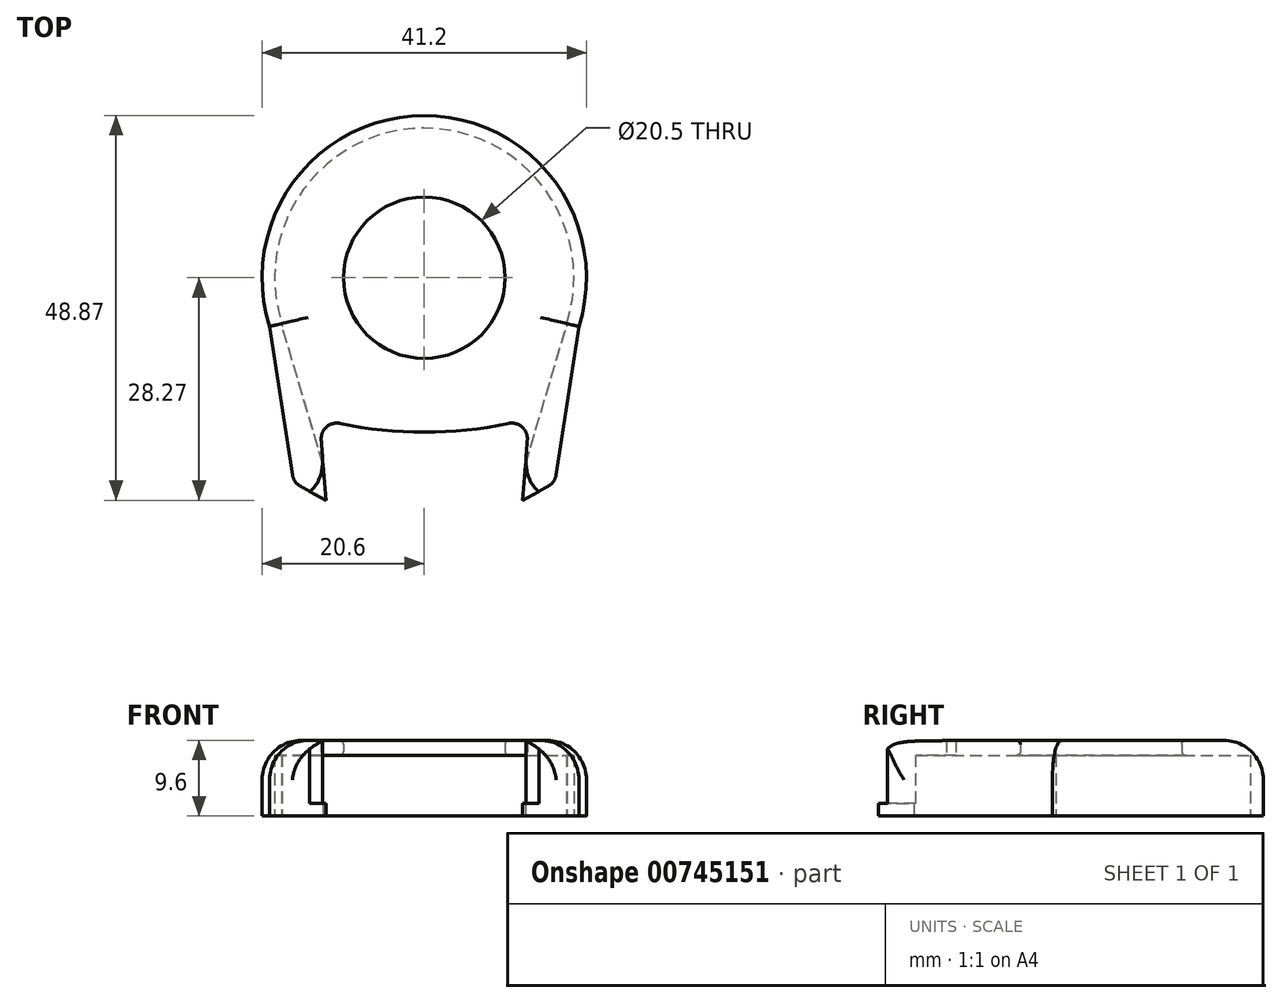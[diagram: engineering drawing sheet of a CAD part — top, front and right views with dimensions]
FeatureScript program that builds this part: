
annotation { "Feature Type Name" : "Feature", "Feature Type Description" : "" }
export const myFeature = defineFeature(function(context is Context, id is Id, definition is map)
    precondition{}
    {
        {
            var Q0;
            Q0=qCreatedBy(makeId("Top.planeOp"),FACE);
            var sketch = newSketch(context, id + "F0", { "sketchPlane" : qUnion([Q0])});
            skCircle(sketch, "E0", {"center": v(0, 0) * mm, "radius": 10.25 * mm});
            skArc(sketch, "E1", {"start": v(7.94, -19) * mm, "mid": v(0, 20.6) * mm, "end": v(-7.94, -19) * mm});
            skLineSegment(sketch, "E2", {"start": v(20.6, 0) * mm, "end": v(20.6, -26) * mm, "construction": true});
            skLineSegment(sketch, "E3", {"start": v(20.6, -26) * mm, "end": v(16.6, -26) * mm, "construction": true});
            skLineSegment(sketch, "E4", {"start": v(16.75, -25.03) * mm, "end": v(19.65, -6.2) * mm});
            skLineSegment(sketch, "E5", {"start": v(15.74, -26.48) * mm, "end": v(12.5, -28.27) * mm});
            skLineSegment(sketch, "E6", {"start": v(17.74, -18.56) * mm, "end": v(13.3, -17.88) * mm, "construction": true});
            skLineSegment(sketch, "E7", {"start": v(12.5, -28.27) * mm, "end": v(13.09, -20.61) * mm});
            skLineSegment(sketch, "E8", {"start": v(13.3, -17.88) * mm, "end": v(0, -17.88) * mm, "construction": true});
            skLineSegment(sketch, "E9.MirrorCS", {"start": v(-13.3, -17.88) * mm, "end": v(0, -17.88) * mm, "construction": true});
            skLineSegment(sketch, "E10.MirrorCS", {"start": v(-12.5, -28.27) * mm, "end": v(-13.09, -20.61) * mm});
            skLineSegment(sketch, "E11.MirrorCS", {"start": v(-15.74, -26.48) * mm, "end": v(-12.5, -28.27) * mm});
            skLineSegment(sketch, "E12.MirrorCS", {"start": v(-16.75, -25.03) * mm, "end": v(-19.65, -6.2) * mm});
            skArc(sketch, "E13", {"start": v(-10.68, -18.5) * mm, "mid": v(0, -19.63) * mm, "end": v(10.68, -18.5) * mm});
            skPoint(sketch, "E14.visualSharp", {"position": v(13.3, -17.88) * mm});
            skArc(sketch, "E14.filletArc", {"start": v(13.09, -20.61) * mm, "mid": v(12.41, -18.96) * mm, "end": v(10.68, -18.5) * mm});
            skPoint(sketch, "E15.visualSharp", {"position": v(-13.3, -17.88) * mm});
            skArc(sketch, "E15.filletArc", {"start": v(-10.68, -18.5) * mm, "mid": v(-12.41, -18.96) * mm, "end": v(-13.09, -20.61) * mm});
            skPoint(sketch, "E16.visualSharp", {"position": v(16.6, -26) * mm});
            skArc(sketch, "E16.filletArc", {"start": v(15.74, -26.48) * mm, "mid": v(16.41, -25.87) * mm, "end": v(16.75, -25.03) * mm});
            skPoint(sketch, "E17.visualSharp", {"position": v(-16.6, -26) * mm});
            skArc(sketch, "E17.filletArc", {"start": v(-16.75, -25.03) * mm, "mid": v(-16.41, -25.87) * mm, "end": v(-15.74, -26.48) * mm});
            skSolve(sketch);
        }
        {
            var Q0;
            Q0 = qSketchRegion(id + "F0", true);
            extrude(context, id + "F1", {"entities" : qUnion([Q0]), "depth" : 9.6 * mm, "offsetDistance" : 25 * mm});
        }
        {
            var Q0;
            Q0=makeQuery(id+"F1.opExtrude","CAP_FACE",FACE,{"disambiguationData":[OSD([sQuery(id+"F0.wireOp",EDGE,"E0"),sQuery(id+"F0.wireOp",EDGE,"E1"),sQuery(id+"F0.wireOp",EDGE,"E4"),sQuery(id+"F0.wireOp",EDGE,"E5"),sQuery(id+"F0.wireOp",EDGE,"E7"),sQuery(id+"F0.wireOp",EDGE,"E10.MirrorCS"),sQuery(id+"F0.wireOp",EDGE,"E11.MirrorCS"),sQuery(id+"F0.wireOp",EDGE,"E12.MirrorCS"),sQuery(id+"F0.wireOp",EDGE,"E13"),sQuery(id+"F0.wireOp",EDGE,"E14.filletArc"),sQuery(id+"F0.wireOp",EDGE,"E15.filletArc"),sQuery(id+"F0.wireOp",EDGE,"E16.filletArc"),sQuery(id+"F0.wireOp",EDGE,"E17.filletArc")])],"isStart":false});
            var sketch = newSketch(context, id + "F2", { "sketchPlane" : qUnion([Q0])});
            skFitSpline(sketch, "E18", {"points": [v(12.93, -22.71) * mm, v(14.55, -27.13) * mm], "startDerivative": vector(-0.4, -5.18) * mm, "endDerivative": vector(3.59, -2.42) * mm});
            skLineSegment(sketch, "E19", {"start": v(14.55, -27.13) * mm, "end": v(14.55, -30.81) * mm});
            skLineSegment(sketch, "E20", {"start": v(14.55, -30.81) * mm, "end": v(10.68, -30.81) * mm});
            skLineSegment(sketch, "E21", {"start": v(10.68, -30.81) * mm, "end": v(10.68, -22.32) * mm});
            skLineSegment(sketch, "E22", {"start": v(10.68, -22.32) * mm, "end": v(12.93, -22.71) * mm});
            skLineSegment(sketch, "E23.MirrorCS", {"start": v(-10.68, -22.32) * mm, "end": v(-12.93, -22.71) * mm});
            skLineSegment(sketch, "E24.MirrorCS", {"start": v(-10.68, -30.81) * mm, "end": v(-10.68, -22.32) * mm});
            skFitSpline(sketch, "E25.MirrorCS", {"points": [v(-12.93, -22.71) * mm, v(-14.55, -27.13) * mm], "startDerivative": vector(0.4, -5.18) * mm, "endDerivative": vector(-3.59, -2.42) * mm});
            skLineSegment(sketch, "E26.MirrorCS", {"start": v(-14.55, -27.13) * mm, "end": v(-14.55, -30.81) * mm});
            skLineSegment(sketch, "E27.MirrorCS", {"start": v(-14.55, -30.81) * mm, "end": v(-10.68, -30.81) * mm});
            skSolve(sketch);
        }
        {
            var Q0;
            Q0 = qSketchRegion(id + "F2", true);
            extrude(context, id + "F3", {"entities" : qUnion([Q0]), "operationType" : NewBodyOperationType.REMOVE, "oppositeDirection" : true, "depth" : 8 * mm, "offsetDistance" : 25 * mm});
        }
        {
            var Q0;
            Q0=makeQuery(id+"F1.opExtrude","CAP_FACE",FACE,{"disambiguationData":[OSD([sQuery(id+"F0.wireOp",EDGE,"E0"),sQuery(id+"F0.wireOp",EDGE,"E1"),sQuery(id+"F0.wireOp",EDGE,"E4"),sQuery(id+"F0.wireOp",EDGE,"E5"),sQuery(id+"F0.wireOp",EDGE,"E7"),sQuery(id+"F0.wireOp",EDGE,"E10.MirrorCS"),sQuery(id+"F0.wireOp",EDGE,"E11.MirrorCS"),sQuery(id+"F0.wireOp",EDGE,"E12.MirrorCS"),sQuery(id+"F0.wireOp",EDGE,"E13"),sQuery(id+"F0.wireOp",EDGE,"E14.filletArc"),sQuery(id+"F0.wireOp",EDGE,"E15.filletArc"),sQuery(id+"F0.wireOp",EDGE,"E16.filletArc"),sQuery(id+"F0.wireOp",EDGE,"E17.filletArc")])],"isStart":true});
            var sketch = newSketch(context, id + "F4", { "sketchPlane" : qUnion([Q0])});
            skPoint(sketch, "E28", {"position": v(12.85, 23.75) * mm});
            skPoint(sketch, "E29", {"position": v(19.65, 6.2) * mm});
            skLineSegment(sketch, "E30", {"start": v(18.05, 6.2) * mm, "end": v(19.65, 6.2) * mm, "construction": true});
            skLineSegment(sketch, "E31", {"start": v(12.85, 23.75) * mm, "end": v(18.05, 6.2) * mm});
            skArc(sketch, "E32.0", {"start": v(18.12, 5.71) * mm, "mid": v(0, -19) * mm, "end": v(-18.12, 5.71) * mm});
            skLineSegment(sketch, "E33", {"start": v(18.12, 5.71) * mm, "end": v(18.05, 6.2) * mm});
            skLineSegment(sketch, "E34.MirrorCS", {"start": v(-18.12, 5.71) * mm, "end": v(-18.05, 6.2) * mm});
            skLineSegment(sketch, "E35.MirrorCS", {"start": v(-12.85, 23.75) * mm, "end": v(-18.05, 6.2) * mm});
            skLineSegment(sketch, "E36", {"start": v(12.85, 23.75) * mm, "end": v(-12.85, 23.75) * mm});
            skSolve(sketch);
        }
        {
            var Q0;
            Q0 = qSketchRegion(id + "F4", true);
            extrude(context, id + "F5", {"entities" : qUnion([Q0]), "operationType" : NewBodyOperationType.REMOVE, "oppositeDirection" : true, "depth" : 7.7 * mm, "offsetDistance" : 25 * mm});
        }
        {
            var Q0;
            Q0=makeQuery(id+"F1.opExtrude","SWEPT_FACE",FACE,{"disambiguationData":[OSD([sQuery(id+"F0.wireOp",EDGE,"E0")])]});
            fillet(context, id + "F6", {"entities" : qUnion([Q0]), "radius" : 0.5 * mm, "tangentPropagation" : true, "allowEdgeOverflow" : false});
        }
        {
            var Q0;
            Q0=makeQuery(id+"F1.opExtrude","CAP_EDGE",EDGE,{"disambiguationData":[OSD([sQuery(id+"F0.wireOp",EDGE,"E1")])],"isStart":false});
            var Q1;
            Q1=makeQuery(id+"F1.opExtrude","CAP_EDGE",EDGE,{"disambiguationData":[OSD([sQuery(id+"F0.wireOp",EDGE,"E4")])],"isStart":false});
            var Q2;
            Q2=makeQuery(id+"F1.opExtrude","CAP_EDGE",EDGE,{"disambiguationData":[OSD([sQuery(id+"F0.wireOp",EDGE,"E12.MirrorCS")])],"isStart":false});
            fillet(context, id + "F7", {"entities" : qUnion([Q0, Q1, Q2]), "radius" : 5 * mm, "tangentPropagation" : true, "allowEdgeOverflow" : false});
        }
    });
